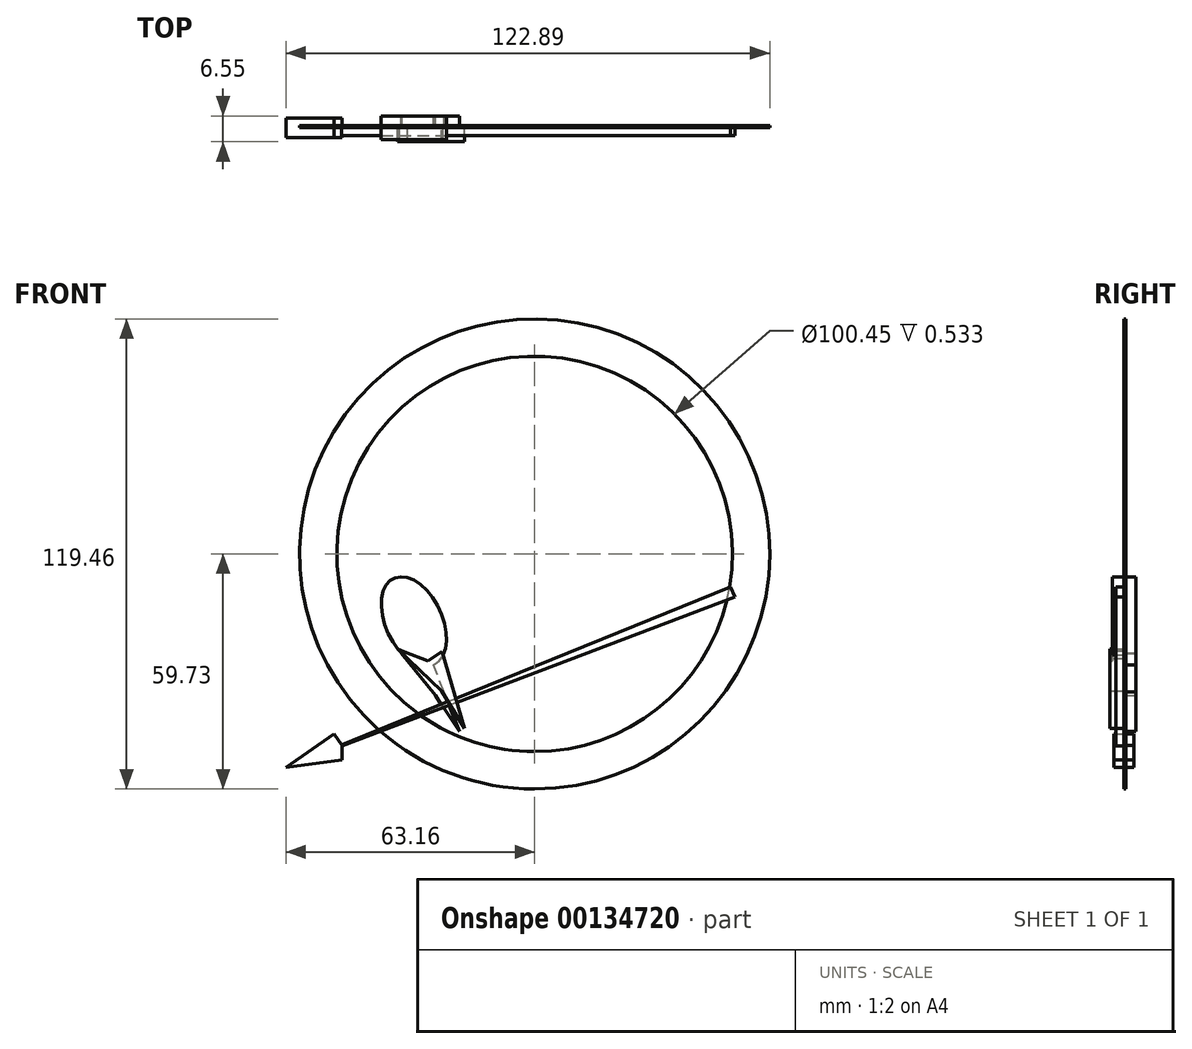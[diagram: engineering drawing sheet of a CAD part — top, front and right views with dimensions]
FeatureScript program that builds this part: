
annotation { "Feature Type Name" : "Feature", "Feature Type Description" : "" }
export const myFeature = defineFeature(function(context is Context, id is Id, definition is map)
    precondition{}
    {
        {
            var Q0;
            Q0=qCreatedBy(makeId("Front.planeOp"),FACE);
            var sketch = newSketch(context, id + "F0", { "sketchPlane" : qUnion([Q0])});
            skCircle(sketch, "E0", {"center": v(0, 0) * mm, "radius": 59.73 * mm});
            skCircle(sketch, "E1", {"center": v(0, 0) * mm, "radius": 50.23 * mm});
            skSolve(sketch);
        }
        {
            var Q0;
            Q0 = qSketchRegion(id + "F0", true);
            extrude(context, id + "F1", {"entities" : qUnion([Q0]), "depth" : 0.03 * mm, "hasSecondDirection" : true, "secondDirectionOppositeDirection" : true, "secondDirectionDepth" : 0.5 * mm});
        }
        {
            var Q0;
            Q0=qCreatedBy(makeId("Front.planeOp"),FACE);
            var sketch = newSketch(context, id + "F2", { "sketchPlane" : qUnion([Q0])});
            skEllipse(sketch, "E2", {"center": v(-30.67, -17.16) * mm, "majorRadius": 12.09 * mm, "minorRadius": 7.2 * mm, "majorAxis": v(0.43, -0.9)});
            skSolve(sketch);
        }
        {
            var Q0;
            Q0 = qSketchRegion(id + "F2", true);
            extrude(context, id + "F3", {"entities" : qUnion([Q0]), "depth" : 3 * mm, "hasSecondDirection" : true, "secondDirectionOppositeDirection" : true, "secondDirectionDepth" : 3 * mm});
        }
        {
            var Q0;
            Q0=qCreatedBy(makeId("Front.planeOp"),FACE);
            var sketch = newSketch(context, id + "F4", { "sketchPlane" : qUnion([Q0])});
            skLineSegment(sketch, "E3", {"start": v(-34, -25.21) * mm, "end": v(-25.2, -35.98) * mm});
            skLineSegment(sketch, "E4", {"start": v(-25.2, -35.98) * mm, "end": v(-19.13, -45.1) * mm});
            skLineSegment(sketch, "E5", {"start": v(-19.13, -45.1) * mm, "end": v(-23.08, -35.07) * mm});
            skLineSegment(sketch, "E6", {"start": v(-23.08, -35.07) * mm, "end": v(-26.11, -26.87) * mm});
            skLineSegment(sketch, "E7", {"start": v(-26.11, -26.87) * mm, "end": v(-34, -25.21) * mm});
            skSolve(sketch);
        }
        {
            var Q0;
            Q0 = qSketchRegion(id + "F4", true);
            extrude(context, id + "F5", {"entities" : qUnion([Q0]), "operationType" : NewBodyOperationType.ADD, "depth" : 0.03 * mm, "hasSecondDirection" : true, "secondDirectionOppositeDirection" : true, "secondDirectionDepth" : 3 * mm});
        }
        {
            var Q0;
            Q0=qCreatedBy(makeId("Front.planeOp"),FACE);
            var sketch = newSketch(context, id + "F6", { "sketchPlane" : qUnion([Q0])});
            skLineSegment(sketch, "E8", {"start": v(-33.1, -24.88) * mm, "end": v(-27.02, -27.22) * mm});
            skLineSegment(sketch, "E9", {"start": v(-27.02, -27.22) * mm, "end": v(-23.49, -24.81) * mm});
            skLineSegment(sketch, "E10", {"start": v(-23.49, -24.81) * mm, "end": v(-17.76, -44.32) * mm});
            skLineSegment(sketch, "E11", {"start": v(-17.76, -44.32) * mm, "end": v(-23.63, -34.78) * mm});
            skLineSegment(sketch, "E12", {"start": v(-23.63, -34.78) * mm, "end": v(-34.8, -24.18) * mm});
            skLineSegment(sketch, "E13", {"start": v(-34.8, -24.18) * mm, "end": v(-33.1, -24.88) * mm});
            skLineSegment(sketch, "E14", {"start": v(-27.02, -27.22) * mm, "end": v(-17.76, -44.32) * mm});
            skSolve(sketch);
        }
        {
            var Q0;
            Q0 = qSketchRegion(id + "F6", true);
            extrude(context, id + "F7", {"entities" : qUnion([Q0]), "operationType" : NewBodyOperationType.ADD, "depth" : 3.55 * mm});
        }
        {
            var Q0;
            Q0=qCreatedBy(makeId("Front.planeOp"),FACE);
            var sketch = newSketch(context, id + "F8", { "sketchPlane" : qUnion([Q0])});
            skLineSegment(sketch, "E15", {"start": v(-63.16, -54.2) * mm, "end": v(49.8, -8.35) * mm});
            skLineSegment(sketch, "E16", {"start": v(49.8, -8.35) * mm, "end": v(50.84, -10.9) * mm});
            skLineSegment(sketch, "E17", {"start": v(50.84, -10.9) * mm, "end": v(-63.16, -54.2) * mm});
            skSolve(sketch);
        }
        {
            var Q0;
            Q0 = qSketchRegion(id + "F8", true);
            extrude(context, id + "F9", {"entities" : qUnion([Q0]), "depth" : 2 * mm});
        }
        {
            var Q0;
            Q0=qCreatedBy(makeId("Front.planeOp"),FACE);
            var sketch = newSketch(context, id + "F10", { "sketchPlane" : qUnion([Q0])});
            skLineSegment(sketch, "E18", {"start": v(-63.16, -54.2) * mm, "end": v(-51.01, -45.7) * mm});
            skLineSegment(sketch, "E19", {"start": v(-51.01, -45.7) * mm, "end": v(-48.93, -48.67) * mm});
            skLineSegment(sketch, "E20", {"start": v(-48.93, -48.67) * mm, "end": v(-48.93, -52.38) * mm});
            skLineSegment(sketch, "E21", {"start": v(-48.93, -52.38) * mm, "end": v(-63.16, -54.2) * mm});
            skSolve(sketch);
        }
        {
            var Q0;
            Q0=makeQuery(id+"F10.imprint","IMPRINT",FACE,{"disambiguationData":[TD([[makeQuery(id+"F10.imprint","IMPRINT",EDGE,{"derivedFrom":sQuery(id+"F10.wireOp",EDGE,"E18")}),-1.0]])]});
            extrude(context, id + "F11", {"entities" : qUnion([Q0]), "operationType" : NewBodyOperationType.ADD, "depth" : 2.5 * mm, "hasSecondDirection" : true, "secondDirectionOppositeDirection" : true, "secondDirectionDepth" : 2.5 * mm});
        }
    });
